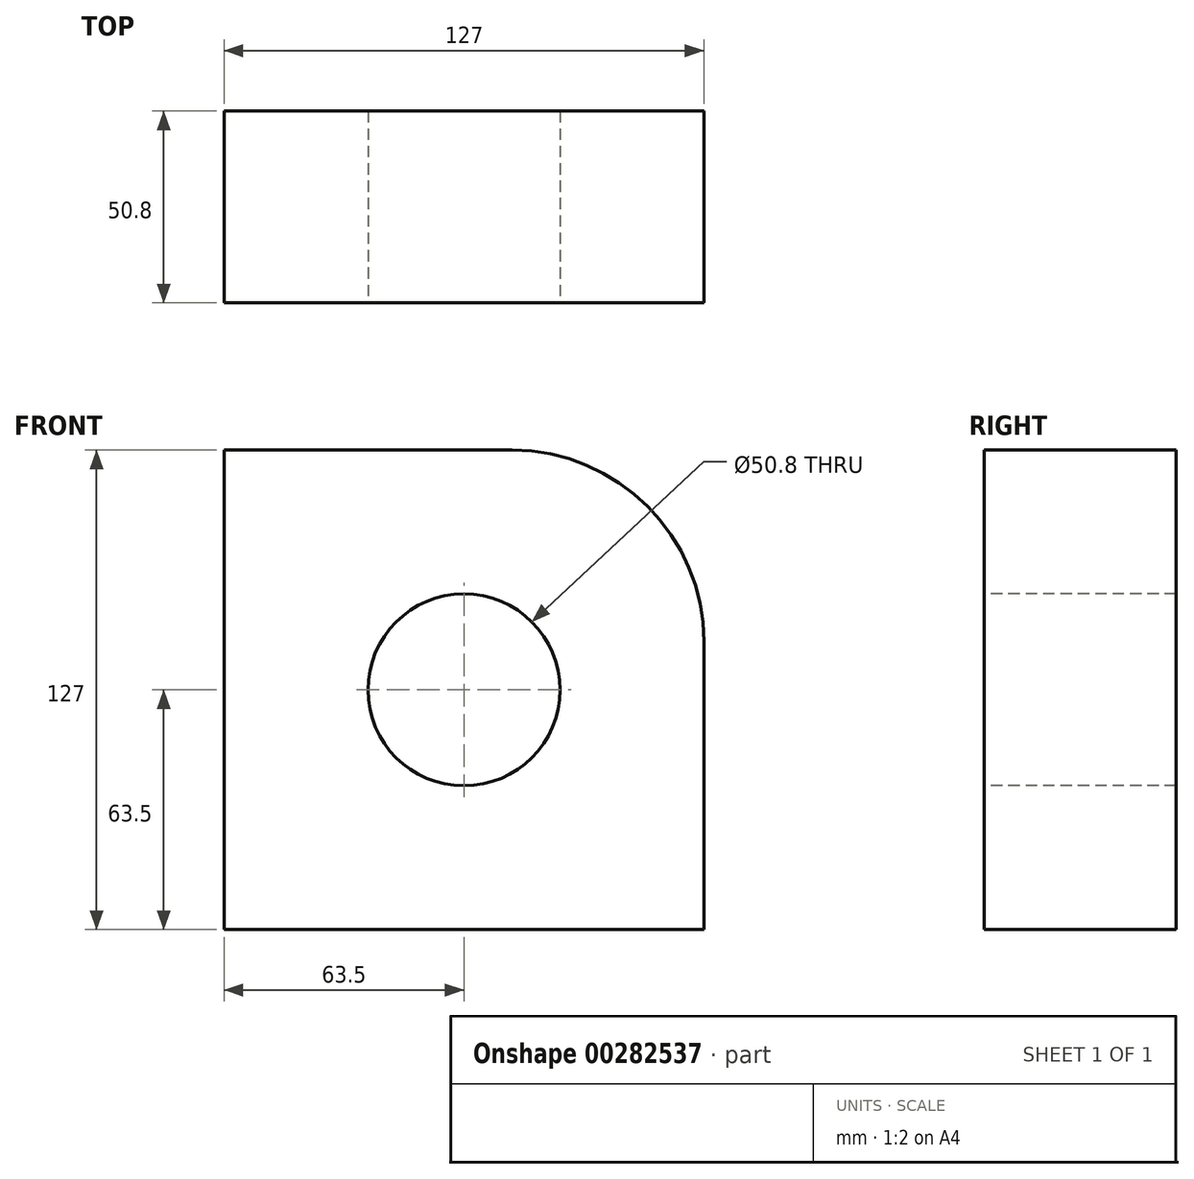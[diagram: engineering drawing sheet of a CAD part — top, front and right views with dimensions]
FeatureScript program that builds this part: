
annotation { "Feature Type Name" : "Feature", "Feature Type Description" : "" }
export const myFeature = defineFeature(function(context is Context, id is Id, definition is map)
    precondition{}
    {
        {
            var Q0;
            Q0=qCreatedBy(makeId("Top.planeOp"),FACE);
            var sketch = newSketch(context, id + "F0", { "sketchPlane" : qUnion([Q0])});
            skLineSegment(sketch, "E0.bottom", {"start": v(-63.5, -25.4) * mm, "end": v(63.5, -25.4) * mm});
            skLineSegment(sketch, "E0.top", {"start": v(-63.5, 25.4) * mm, "end": v(63.5, 25.4) * mm});
            skLineSegment(sketch, "E0.left", {"start": v(-63.5, -25.4) * mm, "end": v(-63.5, 25.4) * mm});
            skLineSegment(sketch, "E0.right", {"start": v(63.5, -25.4) * mm, "end": v(63.5, 25.4) * mm});
            skPoint(sketch, "E0.middle", {"position": v(0, 0) * mm});
            skSolve(sketch);
        }
        {
            var Q0;
            Q0=makeQuery(id+"F0.imprint","IMPRINT",FACE,{"disambiguationData":[TD([[makeQuery(id+"F0.imprint","IMPRINT",EDGE,{"derivedFrom":sQuery(id+"F0.wireOp",EDGE,"E0.bottom")}),1.0]])]});
            extrude(context, id + "F1", {"entities" : qUnion([Q0]), "endBound" : BoundingType.SYMMETRIC, "oppositeDirection" : true, "depth" : 127 * mm});
        }
        {
            var Q0;
            Q0=makeQuery(id+"F1.opExtrude","CAP_EDGE",EDGE,{"disambiguationData":[OSD([sQuery(id+"F0.wireOp",EDGE,"E0.right")])],"isStart":true});
            fillet(context, id + "F2", {"entities" : qUnion([Q0]), "radius" : 50.8 * mm, "tangentPropagation" : true, "allowEdgeOverflow" : false});
        }
        {
            var Q0;
            Q0=makeQuery(id+"F1.opExtrude","SWEPT_FACE",FACE,{"disambiguationData":[OSD([sQuery(id+"F0.wireOp",EDGE,"E0.bottom")])]});
            var sketch = newSketch(context, id + "F3", { "sketchPlane" : qUnion([Q0])});
            skCircle(sketch, "E1", {"center": v(0, 0) * mm, "radius": 25.4 * mm});
            skSolve(sketch);
        }
        {
            var Q0;
            Q0=makeQuery(id+"F3.imprint","IMPRINT",FACE,{"disambiguationData":[TD([[makeQuery(id+"F3.imprint","IMPRINT",EDGE,{"derivedFrom":sQuery(id+"F3.wireOp",EDGE,"E1")}),1.0]])]});
            extrude(context, id + "F4", {"entities" : qUnion([Q0]), "operationType" : NewBodyOperationType.REMOVE, "endBound" : BoundingType.THROUGH_ALL, "oppositeDirection" : true, "depth" : 25.4 * mm});
        }
    });
